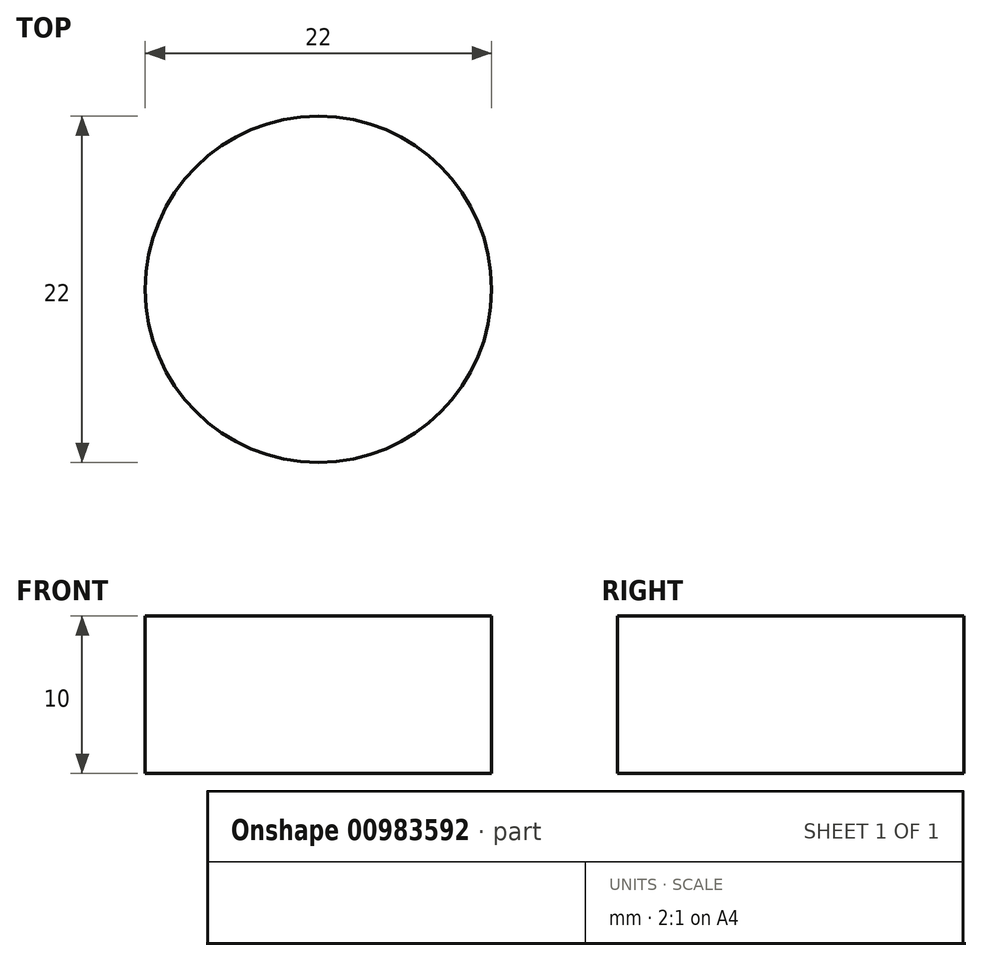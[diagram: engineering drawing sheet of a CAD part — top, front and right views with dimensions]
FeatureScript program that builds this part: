
annotation { "Feature Type Name" : "Feature", "Feature Type Description" : "" }
export const myFeature = defineFeature(function(context is Context, id is Id, definition is map)
    precondition{}
    {
        {
            var Q0;
            Q0=qCreatedBy(makeId("Top.planeOp"),FACE);
            var sketch = newSketch(context, id + "F0", { "sketchPlane" : qUnion([Q0])});
            skCircle(sketch, "E0", {"center": v(0, 0) * mm, "radius": 11 * mm});
            skSolve(sketch);
        }
        {
            var Q0;
            Q0=makeQuery(id+"F0.imprint","IMPRINT",FACE,{"disambiguationData":[TD([[makeQuery(id+"F0.imprint","IMPRINT",EDGE,{"derivedFrom":sQuery(id+"F0.wireOp",EDGE,"E0")}),1.0]])]});
            extrude(context, id + "F1", {"entities" : qUnion([Q0]), "depth" : 10 * mm, "offsetDistance" : 25 * mm});
        }
    });
